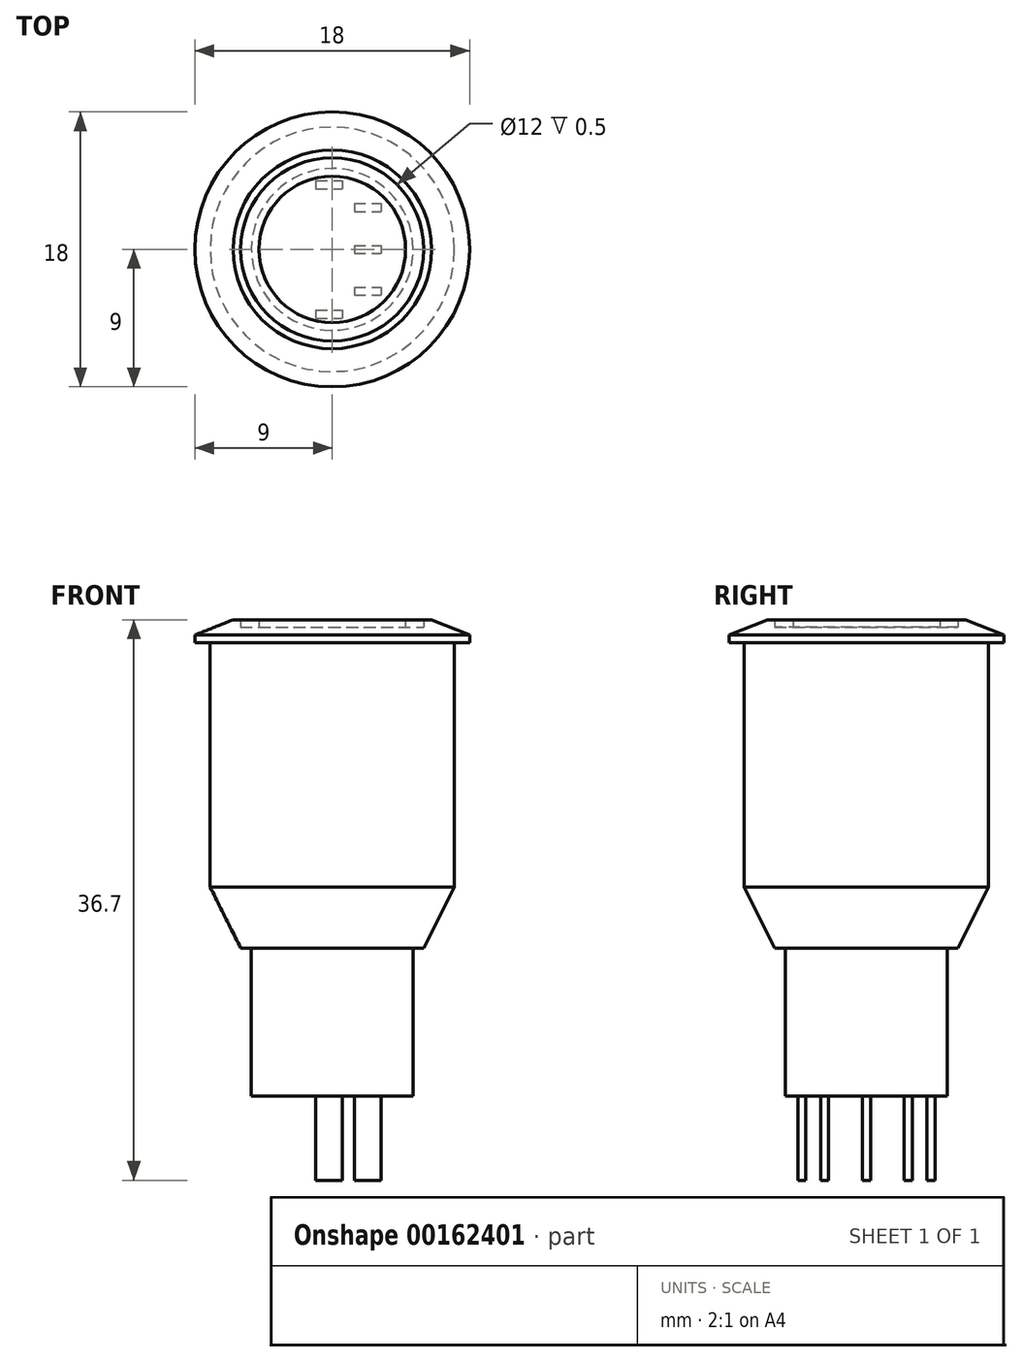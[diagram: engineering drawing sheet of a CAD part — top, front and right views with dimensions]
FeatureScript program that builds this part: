
annotation { "Feature Type Name" : "Feature", "Feature Type Description" : "" }
export const myFeature = defineFeature(function(context is Context, id is Id, definition is map)
    precondition{}
    {
        {
            var Q0;
            Q0=qCreatedBy(makeId("Front.planeOp"),FACE);
            var sketch = newSketch(context, id + "F0", { "sketchPlane" : qUnion([Q0])});
            skLineSegment(sketch, "E0", {"start": v(0, 0) * mm, "end": v(6.5, 0) * mm});
            skLineSegment(sketch, "E1", {"start": v(6.5, 0) * mm, "end": v(9, -1) * mm});
            skLineSegment(sketch, "E2", {"start": v(9, -1) * mm, "end": v(9, -1.5) * mm});
            skLineSegment(sketch, "E3", {"start": v(9, -1.5) * mm, "end": v(8, -1.5) * mm});
            skLineSegment(sketch, "E4", {"start": v(8, -1.5) * mm, "end": v(8, -17.5) * mm});
            skLineSegment(sketch, "E5", {"start": v(8, -17.5) * mm, "end": v(6, -21.5) * mm});
            skLineSegment(sketch, "E6", {"start": v(6, -21.5) * mm, "end": v(5.3, -21.5) * mm});
            skLineSegment(sketch, "E7", {"start": v(5.3, -21.5) * mm, "end": v(5.3, -31.2) * mm});
            skLineSegment(sketch, "E8", {"start": v(5.3, -31.2) * mm, "end": v(0, -31.2) * mm});
            skLineSegment(sketch, "E9", {"start": v(0, -31.2) * mm, "end": v(0, 0) * mm});
            skLineSegment(sketch, "E10.bottom", {"start": v(6, 0) * mm, "end": v(4.8, 0) * mm});
            skLineSegment(sketch, "E10.top", {"start": v(6, -0.5) * mm, "end": v(4.8, -0.5) * mm});
            skLineSegment(sketch, "E10.left", {"start": v(6, 0) * mm, "end": v(6, -0.5) * mm});
            skLineSegment(sketch, "E10.right", {"start": v(4.8, 0) * mm, "end": v(4.8, -0.5) * mm});
            skSolve(sketch);
        }
        {
            var Q0;
            {var subQ4=sQuery(id+"F0.wireOp",EDGE,"E1");Q0=makeQuery(id+"F0.imprint","IMPRINT",FACE,{"disambiguationData":[TD([[makeQuery(id+"F0.imprint","IMPRINT",EDGE,{"derivedFrom":subQ4}),-1.0]])]});}
            var Q1;
            Q1=sQuery(id+"F0.wireOp",EDGE,"E9");
            revolve(context, id + "F1", {"entities" : qUnion([Q0]), "axis" : qUnion([Q1]), "revolveType" : RevolveType.FULL});
        }
        {
            var Q0;
            Q0=makeQuery(id+"F1.opRevolve","SWEPT_FACE",FACE,{"disambiguationData":[OSD([sQuery(id+"F0.wireOp",EDGE,"E8")])]});
            var sketch = newSketch(context, id + "F2", { "sketchPlane" : qUnion([Q0])});
            skLineSegment(sketch, "E11.bottom", {"start": v(-1.08, -4.5) * mm, "end": v(0.67, -4.5) * mm});
            skLineSegment(sketch, "E11.top", {"start": v(-1.08, -3.97) * mm, "end": v(0.67, -3.97) * mm});
            skLineSegment(sketch, "E11.left", {"start": v(-1.08, -4.5) * mm, "end": v(-1.08, -3.97) * mm});
            skLineSegment(sketch, "E11.right", {"start": v(0.67, -4.5) * mm, "end": v(0.67, -3.97) * mm});
            skLineSegment(sketch, "E12.bottom", {"start": v(1.44, -3) * mm, "end": v(3.2, -3) * mm});
            skLineSegment(sketch, "E12.top", {"start": v(1.44, -2.47) * mm, "end": v(3.2, -2.47) * mm});
            skLineSegment(sketch, "E12.left", {"start": v(1.44, -3) * mm, "end": v(1.44, -2.47) * mm});
            skLineSegment(sketch, "E12.right", {"start": v(3.2, -3) * mm, "end": v(3.2, -2.47) * mm});
            skLineSegment(sketch, "E13.bottom", {"start": v(1.44, 2.47) * mm, "end": v(3.2, 2.47) * mm});
            skLineSegment(sketch, "E13.top", {"start": v(1.44, 3) * mm, "end": v(3.2, 3) * mm});
            skLineSegment(sketch, "E13.left", {"start": v(3.2, 2.47) * mm, "end": v(3.2, 3) * mm});
            skLineSegment(sketch, "E13.right", {"start": v(1.44, 2.47) * mm, "end": v(1.44, 3) * mm});
            skLineSegment(sketch, "E14.bottom", {"start": v(-1.08, 3.97) * mm, "end": v(0.67, 3.97) * mm});
            skLineSegment(sketch, "E14.top", {"start": v(-1.08, 4.5) * mm, "end": v(0.67, 4.5) * mm});
            skLineSegment(sketch, "E14.left", {"start": v(-1.08, 3.97) * mm, "end": v(-1.08, 4.5) * mm});
            skLineSegment(sketch, "E14.right", {"start": v(0.67, 3.97) * mm, "end": v(0.67, 4.5) * mm});
            skLineSegment(sketch, "E15", {"start": v(2.32, -2.73) * mm, "end": v(2.32, 2.74) * mm, "construction": true});
            skPoint(sketch, "E15.startSnap0", {"position": v(2.32, -2.47) * mm});
            skPoint(sketch, "E15.startSnap1", {"position": v(1.44, -2.74) * mm});
            skPoint(sketch, "E15.endSnap0", {"position": v(2.32, 3) * mm});
            skPoint(sketch, "E15.endSnap1", {"position": v(3.2, 2.73) * mm});
            skLineSegment(sketch, "E16", {"start": v(-0.2, -4.24) * mm, "end": v(-0.2, 4.24) * mm, "construction": true});
            skPoint(sketch, "E16.startSnap0", {"position": v(-0.2, -3.97) * mm});
            skPoint(sketch, "E16.startSnap1", {"position": v(-1.08, -4.24) * mm});
            skPoint(sketch, "E16.endSnap0", {"position": v(-0.2, 4.5) * mm});
            skPoint(sketch, "E16.endSnap1", {"position": v(-1.08, 4.24) * mm});
            skPoint(sketch, "E17", {"position": v(-0.2, 0) * mm});
            skPoint(sketch, "E18", {"position": v(2.32, 0) * mm});
            skLineSegment(sketch, "E19.bottom", {"start": v(1.44, -0.27) * mm, "end": v(3.2, -0.27) * mm});
            skLineSegment(sketch, "E19.top", {"start": v(1.44, 0.27) * mm, "end": v(3.2, 0.27) * mm});
            skLineSegment(sketch, "E19.left", {"start": v(1.44, -0.27) * mm, "end": v(1.44, 0.27) * mm});
            skLineSegment(sketch, "E19.right", {"start": v(3.2, -0.27) * mm, "end": v(3.2, 0.27) * mm});
            skSolve(sketch);
        }
        {
            var Q0;
            Q0=makeQuery(id+"F2.imprint","IMPRINT",FACE,{"disambiguationData":[TD([[makeQuery(id+"F2.imprint","IMPRINT",EDGE,{"derivedFrom":sQuery(id+"F2.wireOp",EDGE,"E11.bottom")}),1.0]])]});
            var Q1;
            Q1=makeQuery(id+"F2.imprint","IMPRINT",FACE,{"disambiguationData":[TD([[makeQuery(id+"F2.imprint","IMPRINT",EDGE,{"derivedFrom":sQuery(id+"F2.wireOp",EDGE,"E12.bottom")}),1.0]])]});
            var Q2;
            Q2=makeQuery(id+"F2.imprint","IMPRINT",FACE,{"disambiguationData":[TD([[makeQuery(id+"F2.imprint","IMPRINT",EDGE,{"derivedFrom":sQuery(id+"F2.wireOp",EDGE,"E19.bottom")}),1.0]])]});
            var Q3;
            Q3=makeQuery(id+"F2.imprint","IMPRINT",FACE,{"disambiguationData":[TD([[makeQuery(id+"F2.imprint","IMPRINT",EDGE,{"derivedFrom":sQuery(id+"F2.wireOp",EDGE,"E13.bottom")}),1.0]])]});
            var Q4;
            Q4=makeQuery(id+"F2.imprint","IMPRINT",FACE,{"disambiguationData":[TD([[makeQuery(id+"F2.imprint","IMPRINT",EDGE,{"derivedFrom":sQuery(id+"F2.wireOp",EDGE,"E14.bottom")}),1.0]])]});
            extrude(context, id + "F3", {"entities" : qUnion([Q0, Q1, Q2, Q3, Q4]), "operationType" : NewBodyOperationType.ADD, "depth" : 5.5 * mm});
        }
    });
